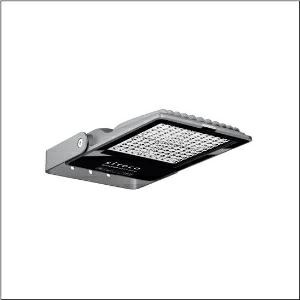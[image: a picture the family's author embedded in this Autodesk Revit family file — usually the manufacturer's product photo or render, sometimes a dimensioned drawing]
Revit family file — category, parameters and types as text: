
# Revit family: sicompact_r__31_mini___pl32_5xa7571c2k23_606d
name_source: partatom
category: Lighting Fixtures
units: mm (PartAtom-declared; Revit-internal decimal feet)

## family parameters
Cut with Voids When Loaded = No
Host = Face
Light Source = No
Part Type = Normal
Room Calculation Point = No
Round Connector Dimension = Use Diameter
Shared = No

## types (1)
- SiCompact® 31 mini  PL32 (1 x LED, 15000 lm, 95 W, 4000K)
    Apparent Load = 95 VA
    CIE Flux Codes = 32 69 98 100 100
    Color Rendering = 70
    Color Temperature = 4000K
    Default Elevation = 1800 mm
    Description = SiCompact® 31 mini, floodlight, primary light control with lens, of plastic, of toughened safety glass, transparent, light distribution: PL32, light emission: direct distribution, primary light characteristic: asymmetric, installation type: surface-mounted, LED, High Power LED, rated luminous flux: 15.000lm, luminous efficacy: 158lm/W, light colour: 740, colour temperature: 4000K, control gear: ECG, with cable, 3x 1.5mm², mains connection: 220..240V, AC, 50/60Hz, connection cable pre-assembled, cable length: 2m, rated input power: 95W, of diecast aluminium, specular, metallic grey (RAL 9006), length: 461mm, width: 261mm, height: 62mm, bracket, of sheet steel, coated, metallic grey (RAL 9006), ON/OFF, protection rating (complete): IP66, insulation class (complete): insulation class I (protective earthing), certification: CE, ENEC, impact resistance: IK08, permissible operating ambient temperature: -40..+45°C, packaging unit: 1 piece

Light Distribution: PL32
    Height = 62 mm  [stored 0.203412 ft]
    Lamp = 1 x LED
    Lamp Light Flux = 15000 lm
    Lamp Power = 95 W
    Lamp count = 1
    Length = 460 mm
    Luminous efficacy = 158 lm/W
    Manufacturer = Siteco
    ModVariant = No
    Model = 5XA7571C2K23
    Mounting Place = Wall
    Mounting Type = Surface mounted
    Number of Poles = 1
    OnlyDefault = Yes
    Power Factor = 1
    Product Name = SiCompact® 31 mini | PL32
    Product group = floodlight | wall mounted
    ProductGroupID = 2001
    Protection Class = Protection class I
    Protection Degree = IP 66
    RLX_Detail_Level = 1
    RLX_Emergency_Light_Flux = 0 lm
    RLX_Emergency_Type = 0
    RLX_Emergency_Type_DB = No
    RlxData = <blob elided: 126065 chars, md5=66484707>
    Socket = socket
    Standby Power = 0 W
    System Light Flux = 15000 lm
    System Power = 95 W
    Type Comments = Product without accessories
    Type Image = l_1006951.jpg
    URL = http://relux.com
    VarID = ---
    Voltage = 0 V
    Weight = 0.00 kg
    Width = 260 mm

note: [stored X ft] marks values corroborated as IEEE doubles in the binary element streams (Revit-internal decimal feet)

## geometry (parser evidence)
native form markers: Blend x4, Sweep x14
no freeform markers — native parametric forms only
